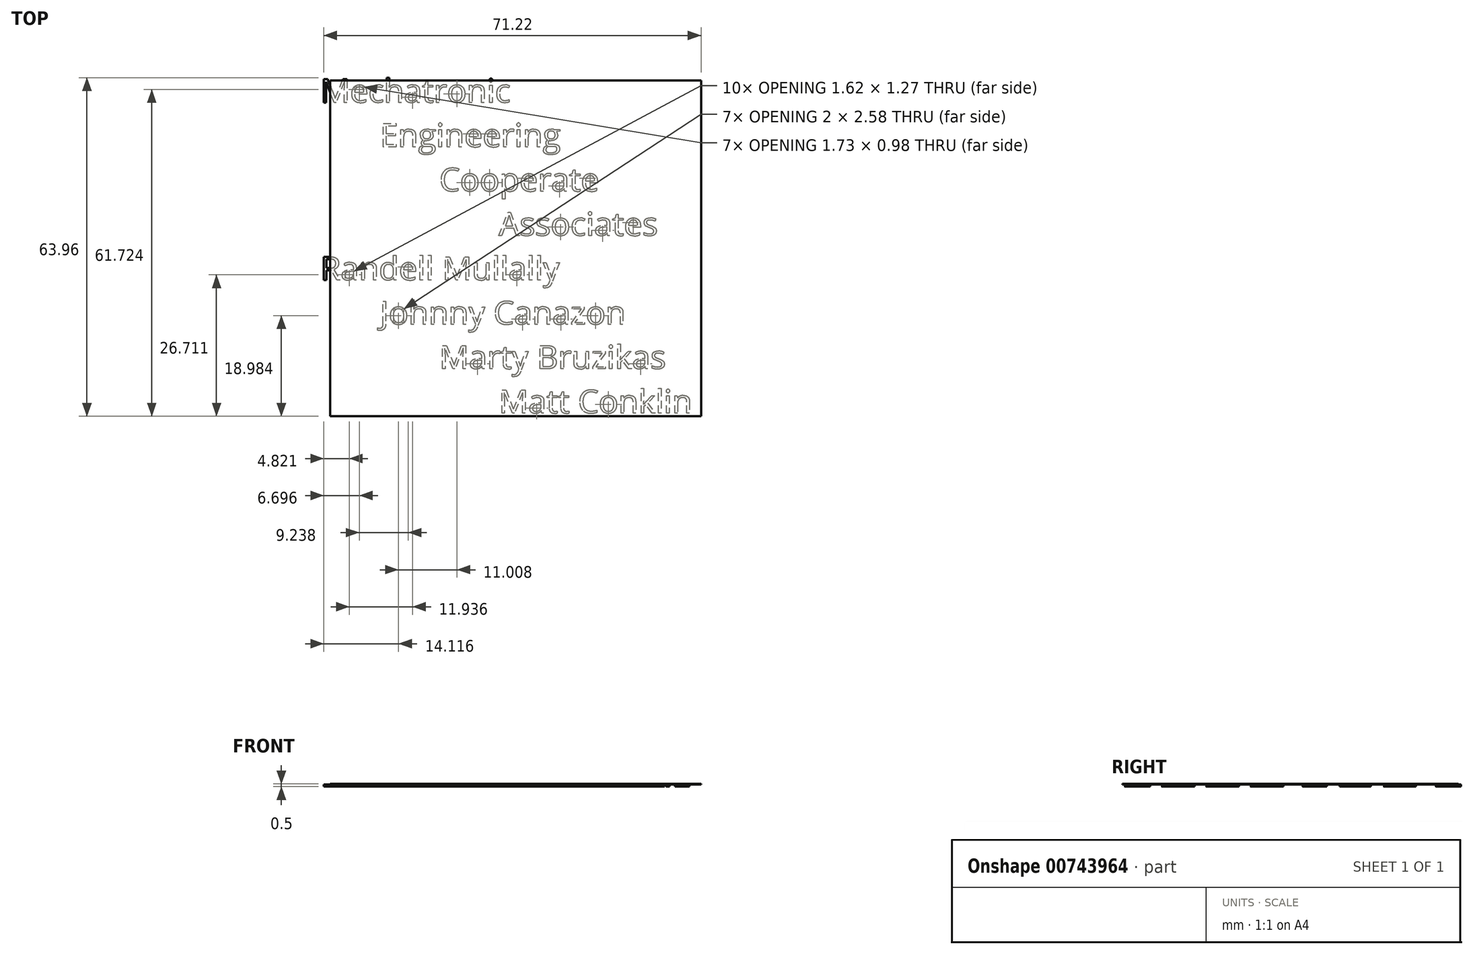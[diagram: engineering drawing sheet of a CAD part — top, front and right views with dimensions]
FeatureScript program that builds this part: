
annotation { "Feature Type Name" : "Feature", "Feature Type Description" : "" }
export const myFeature = defineFeature(function(context is Context, id is Id, definition is map)
    precondition{}
    {
        {
            var Q0;
            Q0=qCreatedBy(makeId("Top.planeOp"),FACE);
            var sketch = newSketch(context, id + "F0", { "sketchPlane" : qUnion([Q0])});
            skText(sketch, "E0", { "text": "Mechatronic\n       Engineering\n              Cooperate \n                     Associates\nRandell Mullally\n       Johnny Canazon\n              Marty Bruzikas \n                     Matt Conklin", "fontName": "OpenSans-Regular.ttf"});
            const initialGuessF0  = {"E0": [-0.0021, -0.00223, 1, 0, 0.00444]};
            skSetInitialGuess(sketch, initialGuessF0);
            skSolve(sketch);
        }
        {
            var Q0;
            Q0 = qSketchRegion(id + "F0", true);
            extrude(context, id + "F1", {"entities" : qUnion([Q0]), "depth" : .4 * mm, "offsetDistance" : 25.4 * mm});
        }
        {
            var Q0;
            Q0=makeQuery(id+"F1.opExtrude","CAP_FACE",FACE,{"disambiguationData":[OSD([sQuery(id+"F0.wireOp",EDGE,"E0.sketch_text.stroke-190"),sQuery(id+"F0.wireOp",EDGE,"E0.sketch_text.stroke-191"),sQuery(id+"F0.wireOp",EDGE,"E0.sketch_text.stroke-192"),sQuery(id+"F0.wireOp",EDGE,"E0.sketch_text.stroke-193"),sQuery(id+"F0.wireOp",EDGE,"E0.sketch_text.stroke-194"),sQuery(id+"F0.wireOp",EDGE,"E0.sketch_text.stroke-195"),sQuery(id+"F0.wireOp",EDGE,"E0.sketch_text.stroke-196"),sQuery(id+"F0.wireOp",EDGE,"E0.sketch_text.stroke-197"),sQuery(id+"F0.wireOp",EDGE,"E0.sketch_text.stroke-198"),sQuery(id+"F0.wireOp",EDGE,"E0.sketch_text.stroke-199"),sQuery(id+"F0.wireOp",EDGE,"E0.sketch_text.stroke-200"),sQuery(id+"F0.wireOp",EDGE,"E0.sketch_text.stroke-201")])],"isStart":false});
            var sketch = newSketch(context, id + "F2", { "sketchPlane" : qUnion([Q0])});
            skLineSegment(sketch, "E1.bottom", {"start": v(-0.27, 1.97) * mm, "end": v(69.73, 1.97) * mm});
            skLineSegment(sketch, "E1.top", {"start": v(-0.27, -61.5) * mm, "end": v(69.73, -61.5) * mm});
            skLineSegment(sketch, "E1.left", {"start": v(-0.27, 1.97) * mm, "end": v(-0.27, -61.5) * mm});
            skLineSegment(sketch, "E1.right", {"start": v(69.73, 1.97) * mm, "end": v(69.73, -61.5) * mm});
            skSolve(sketch);
        }
        {
            var Q0;
            Q0 = qSketchRegion(id + "F2", true);
            extrude(context, id + "F3", {"entities" : qUnion([Q0]), "depth" : .1 * mm, "offsetDistance" : 25.4 * mm});
        }
    });
